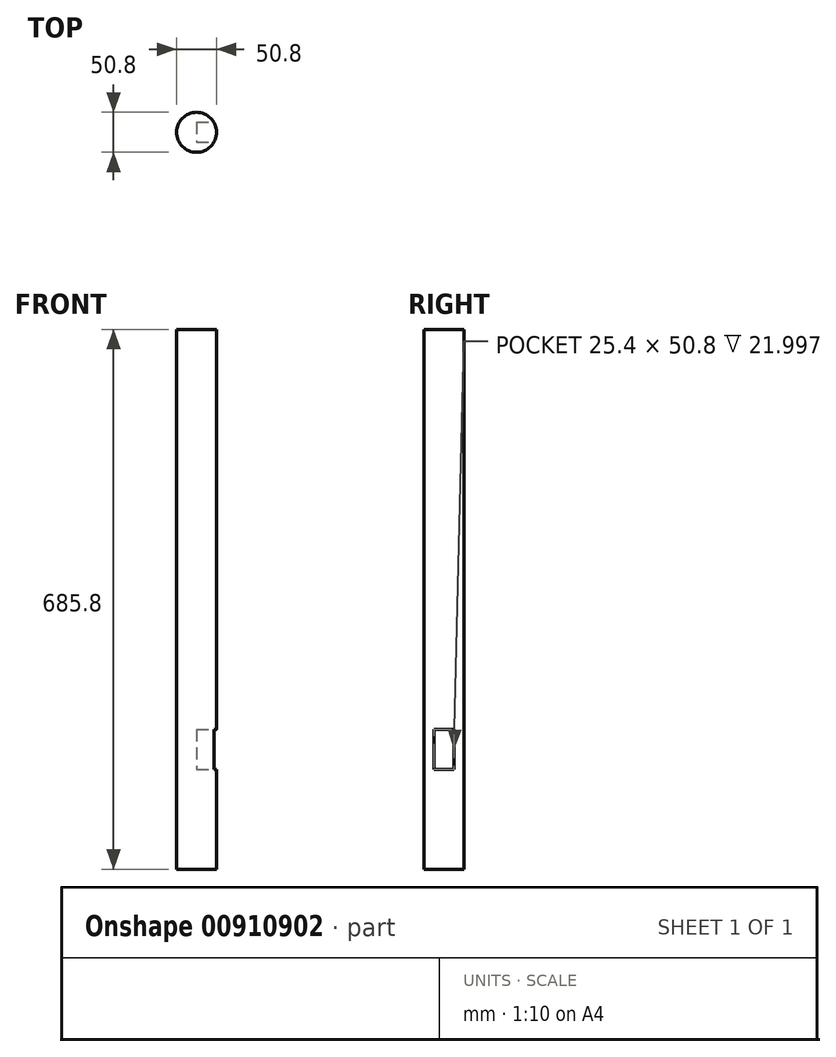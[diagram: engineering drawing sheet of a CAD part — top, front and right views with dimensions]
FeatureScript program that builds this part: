
annotation { "Feature Type Name" : "Feature", "Feature Type Description" : "" }
export const myFeature = defineFeature(function(context is Context, id is Id, definition is map)
    precondition{}
    {
        {
            var Q0;
            Q0=qCreatedBy(makeId("Top.planeOp"),FACE);
            var sketch = newSketch(context, id + "F0", { "sketchPlane" : qUnion([Q0])});
            skCircle(sketch, "E0", {"center": v(0, 0) * mm, "radius": 25.4 * mm});
            skSolve(sketch);
        }
        {
            var Q0;
            Q0 = qSketchRegion(id + "F0", true);
            extrude(context, id + "F1", {"entities" : qUnion([Q0]), "depth" : 228.6 * mm, "offsetDistance" : 25.4 * mm});
        }
        {
            var Q0;
            Q0 = qSketchRegion(id + "F0", true);
            extrude(context, id + "F2", {"entities" : qUnion([Q0]), "operationType" : NewBodyOperationType.ADD, "oppositeDirection" : true, "depth" : 457.2 * mm, "offsetDistance" : 25.4 * mm});
        }
        {
            var Q0;
            Q0=makeQuery(id+"F1.opExtrude","CAP_FACE",FACE,{"disambiguationData":[OSD([sQuery(id+"F0.wireOp",EDGE,"E0")])],"isStart":false});
            var sketch = newSketch(context, id + "F3", { "sketchPlane" : qUnion([Q0])});
            skLineSegment(sketch, "E1", {"start": v(0, 0) * mm, "end": v(25.4, 0) * mm});
            skSolve(sketch);
        }
        {
            var Q0;
            Q0=sQuery(id+"F3.wireOp",EDGE,"E1");
            var Q1;
            Q1=sQuery(id+"F3.wireOp",VERTEX,"E1.end");
            cPlane(context, id + "F4", {"entities" : qUnion([Q0, Q1]), "cplaneType" : CPlaneType.LINE_POINT, "offset" : 25.4 * mm, "width" : 152.4 * mm, "height" : 152.4 * mm});
        }
        {
            var Q0;
            Q0=qCreatedBy(id+"F4.planeOp",FACE);
            var sketch = newSketch(context, id + "F5", { "sketchPlane" : qUnion([Q0])});
            skLineSegment(sketch, "E2.bottom", {"start": v(12.7, -279.68) * mm, "end": v(-12.7, -279.68) * mm});
            skLineSegment(sketch, "E2.top", {"start": v(12.7, -330.48) * mm, "end": v(-12.7, -330.48) * mm});
            skLineSegment(sketch, "E2.left", {"start": v(12.7, -279.68) * mm, "end": v(12.7, -330.48) * mm});
            skLineSegment(sketch, "E2.right", {"start": v(-12.7, -279.68) * mm, "end": v(-12.7, -330.48) * mm});
            skPoint(sketch, "E2.middle", {"position": v(0, -305.08) * mm});
            skSolve(sketch);
        }
        {
            var Q0;
            Q0=makeQuery(id+"F5.imprint","IMPRINT",FACE,{"disambiguationData":[TD([[makeQuery(id+"F5.imprint","IMPRINT",EDGE,{"derivedFrom":sQuery(id+"F5.wireOp",EDGE,"E2.bottom")}),1.0]])]});
            extrude(context, id + "F6", {"entities" : qUnion([Q0]), "operationType" : NewBodyOperationType.REMOVE, "oppositeDirection" : true, "depth" : 25.4 * mm, "offsetDistance" : 25.4 * mm});
        }
    });
